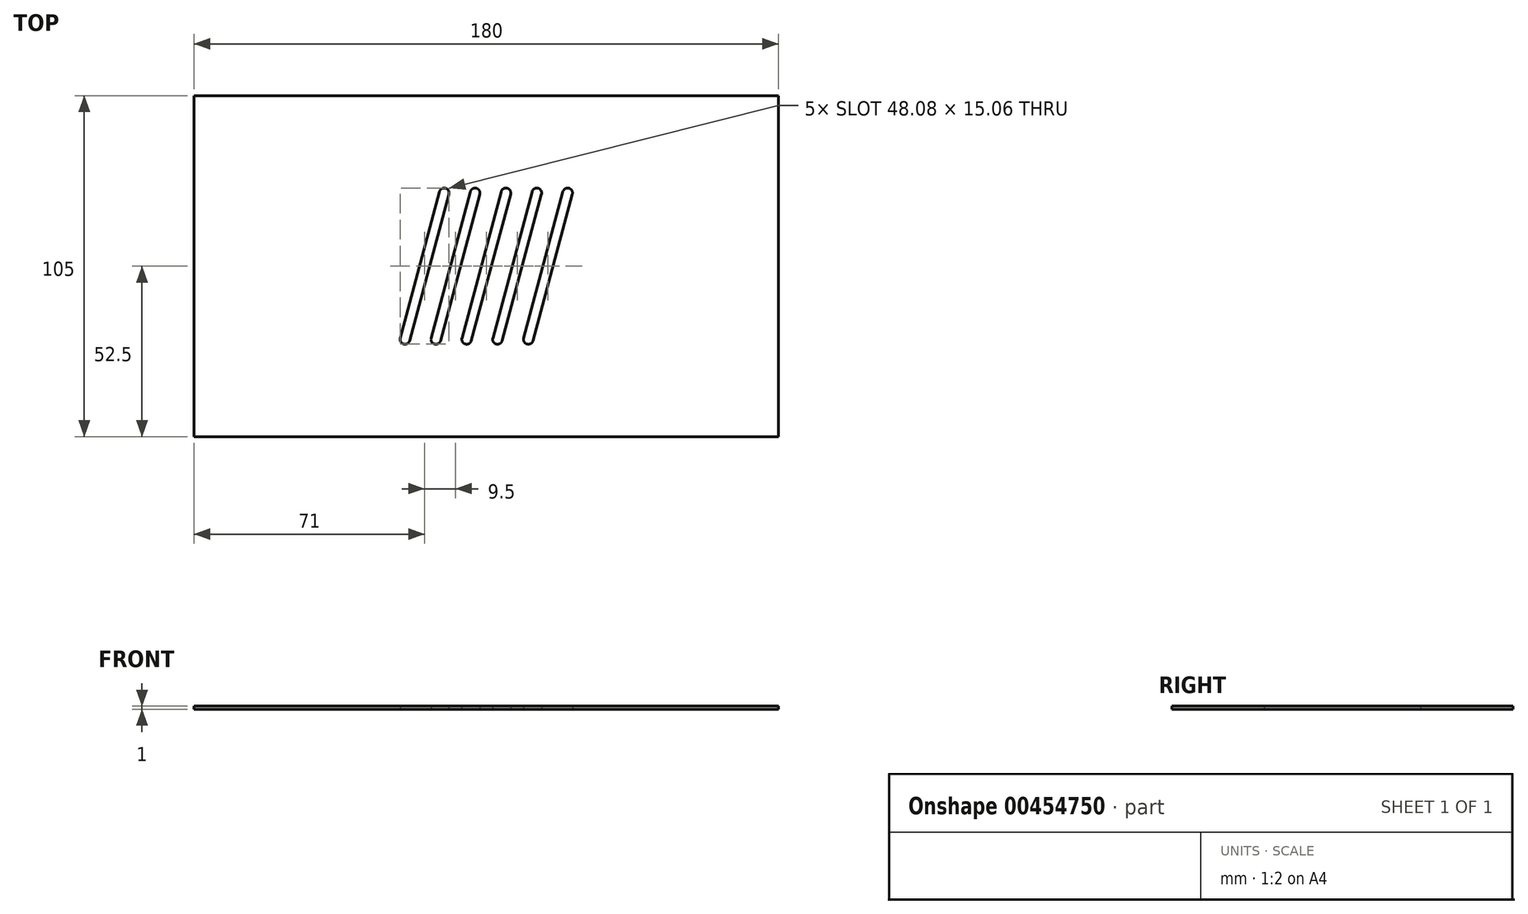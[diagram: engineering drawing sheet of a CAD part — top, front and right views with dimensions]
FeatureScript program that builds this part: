
annotation { "Feature Type Name" : "Feature", "Feature Type Description" : "" }
export const myFeature = defineFeature(function(context is Context, id is Id, definition is map)
    precondition{}
    {
        {
            var Q0;
            Q0=qCreatedBy(makeId("Top.planeOp"),FACE);
            var sketch = newSketch(context, id + "F0", { "sketchPlane" : qUnion([Q0])});
            skLineSegment(sketch, "E0.bottom", {"start": v(90, 52.5) * mm, "end": v(-90, 52.5) * mm});
            skLineSegment(sketch, "E0.top", {"start": v(90, -52.5) * mm, "end": v(-90, -52.5) * mm});
            skLineSegment(sketch, "E0.left", {"start": v(90, 52.5) * mm, "end": v(90, -52.5) * mm});
            skLineSegment(sketch, "E0.right", {"start": v(-90, 52.5) * mm, "end": v(-90, -52.5) * mm});
            skPoint(sketch, "E0.middle", {"position": v(0, 0) * mm});
            skLineSegment(sketch, "E1", {"start": v(-6.43, -24) * mm, "end": v(6.43, 24) * mm, "construction": true});
            skLineSegment(sketch, "E2.0", {"start": v(-4.6, -22.94) * mm, "end": v(7.5, 22.16) * mm});
            skLineSegment(sketch, "E3.0", {"start": v(-7.5, -22.16) * mm, "end": v(4.6, 22.94) * mm});
            skArc(sketch, "E4", {"start": v(7.5, 22.16) * mm, "mid": v(6.43, 24) * mm, "end": v(4.6, 22.94) * mm});
            skArc(sketch, "E5", {"start": v(-7.5, -22.16) * mm, "mid": v(-6.43, -24) * mm, "end": v(-4.6, -22.94) * mm});
            skLineSegment(sketch, "E6.1.0.0", {"start": v(2, -22.16) * mm, "end": v(14.1, 22.94) * mm});
            skLineSegment(sketch, "E6.1.0.1", {"start": v(3.07, -24) * mm, "end": v(15.93, 24) * mm, "construction": true});
            skLineSegment(sketch, "E6.1.0.2", {"start": v(4.9, -22.94) * mm, "end": v(17, 22.16) * mm});
            skPoint(sketch, "E6.1.0.3", {"position": v(9.5, 0) * mm});
            skPoint(sketch, "E6.1.0.4", {"position": v(9.5, 0) * mm});
            skArc(sketch, "E6.1.0.5", {"start": v(17, 22.16) * mm, "mid": v(15.93, 24) * mm, "end": v(14.1, 22.94) * mm});
            skArc(sketch, "E6.1.0.6", {"start": v(2, -22.16) * mm, "mid": v(3.07, -24) * mm, "end": v(4.9, -22.94) * mm});
            skLineSegment(sketch, "E6.2.0.0", {"start": v(11.5, -22.16) * mm, "end": v(23.6, 22.94) * mm});
            skLineSegment(sketch, "E6.2.0.1", {"start": v(12.57, -24) * mm, "end": v(25.43, 24) * mm, "construction": true});
            skLineSegment(sketch, "E6.2.0.2", {"start": v(14.4, -22.94) * mm, "end": v(26.5, 22.16) * mm});
            skPoint(sketch, "E6.2.0.3", {"position": v(19, 0) * mm});
            skPoint(sketch, "E6.2.0.4", {"position": v(19, 0) * mm});
            skArc(sketch, "E6.2.0.5", {"start": v(26.5, 22.16) * mm, "mid": v(25.43, 24) * mm, "end": v(23.6, 22.94) * mm});
            skArc(sketch, "E6.2.0.6", {"start": v(11.5, -22.16) * mm, "mid": v(12.57, -24) * mm, "end": v(14.4, -22.94) * mm});
            skLineSegment(sketch, "E6.direction1", {"start": v(-6.43, -24) * mm, "end": v(3.07, -24) * mm, "construction": true});
            skLineSegment(sketch, "E7.1.0.0", {"start": v(-15.93, -24) * mm, "end": v(-3.07, 24) * mm, "construction": true});
            skArc(sketch, "E7.1.0.1", {"start": v(-17, -22.16) * mm, "mid": v(-15.93, -24) * mm, "end": v(-14.1, -22.94) * mm});
            skLineSegment(sketch, "E7.1.0.2", {"start": v(-14.1, -22.94) * mm, "end": v(-2, 22.16) * mm});
            skLineSegment(sketch, "E7.1.0.3", {"start": v(-17, -22.16) * mm, "end": v(-4.9, 22.94) * mm});
            skArc(sketch, "E7.1.0.4", {"start": v(-2, 22.16) * mm, "mid": v(-3.07, 24) * mm, "end": v(-4.9, 22.94) * mm});
            skLineSegment(sketch, "E7.2.0.0", {"start": v(-25.43, -24) * mm, "end": v(-12.57, 24) * mm, "construction": true});
            skArc(sketch, "E7.2.0.1", {"start": v(-26.5, -22.16) * mm, "mid": v(-25.43, -24) * mm, "end": v(-23.6, -22.94) * mm});
            skLineSegment(sketch, "E7.2.0.2", {"start": v(-23.6, -22.94) * mm, "end": v(-11.5, 22.16) * mm});
            skLineSegment(sketch, "E7.2.0.3", {"start": v(-26.5, -22.16) * mm, "end": v(-14.4, 22.94) * mm});
            skArc(sketch, "E7.2.0.4", {"start": v(-11.5, 22.16) * mm, "mid": v(-12.57, 24) * mm, "end": v(-14.4, 22.94) * mm});
            skLineSegment(sketch, "E7.direction1", {"start": v(-6.43, -24) * mm, "end": v(-15.93, -24) * mm, "construction": true});
            skSolve(sketch);
        }
        {
            var Q0;
            Q0 = qSketchRegion(id + "F0", true);
            extrude(context, id + "F1", {"entities" : qUnion([Q0]), "depth" : 1 * mm});
        }
    });
